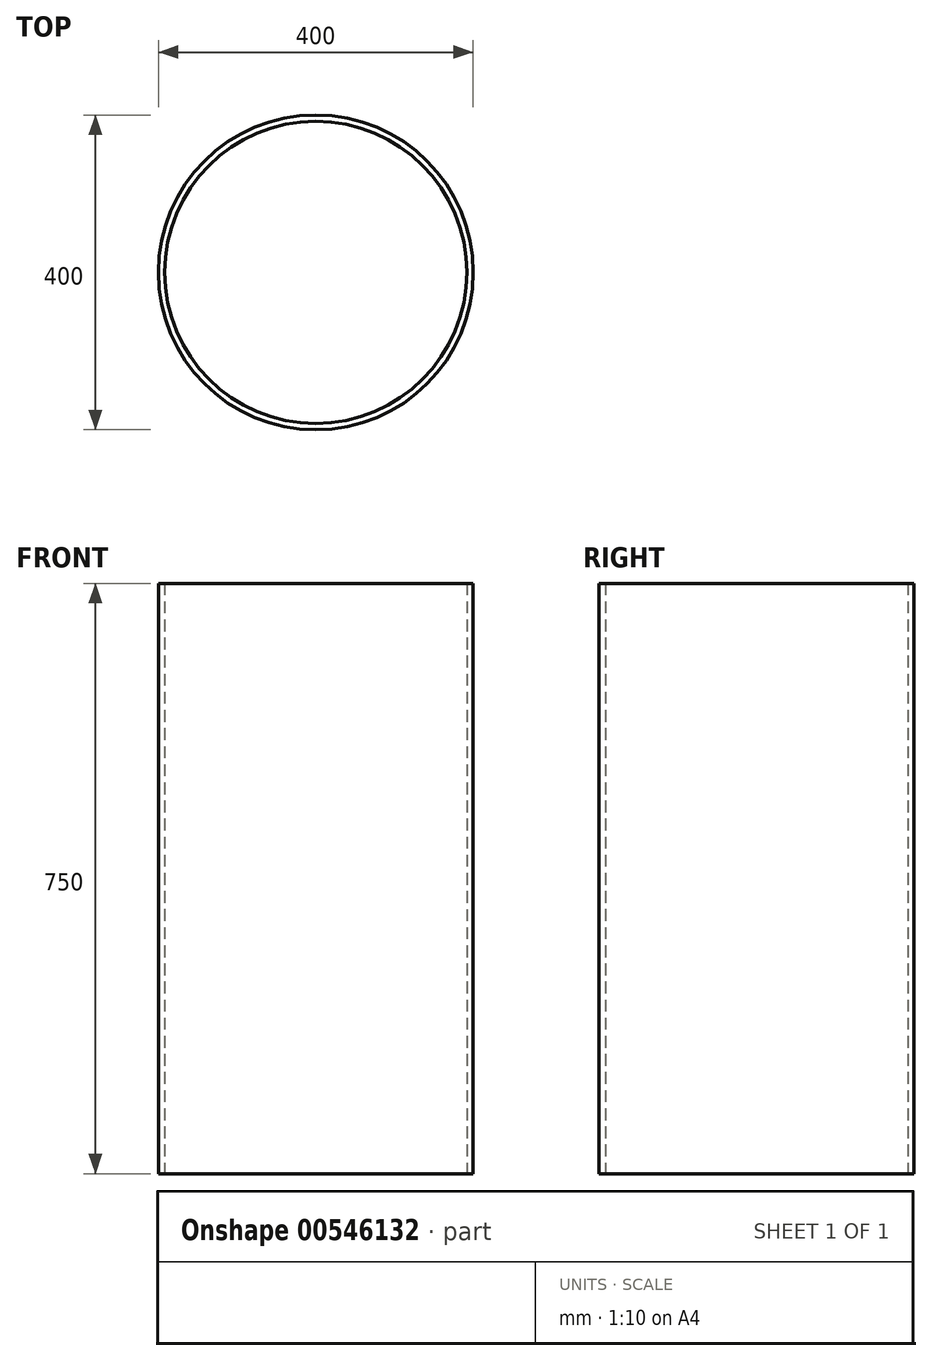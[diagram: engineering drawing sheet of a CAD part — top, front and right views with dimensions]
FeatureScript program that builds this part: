
annotation { "Feature Type Name" : "Feature", "Feature Type Description" : "" }
export const myFeature = defineFeature(function(context is Context, id is Id, definition is map)
    precondition{}
    {
        {
            var Q0;
            Q0=qCreatedBy(makeId("Top.planeOp"),FACE);
            var sketch = newSketch(context, id + "F0", { "sketchPlane" : qUnion([Q0])});
            skCircle(sketch, "E0", {"center": v(0, 0) * mm, "radius": 200 * mm});
            skCircle(sketch, "E1", {"center": v(0, 0) * mm, "radius": 192 * mm});
            skSolve(sketch);
        }
        {
            var Q0;
            Q0 = qSketchRegion(id + "F0", true);
            extrude(context, id + "F1", {"entities" : qUnion([Q0]), "depth" : 750 * mm, "offsetDistance" : 25 * mm});
        }
    });
